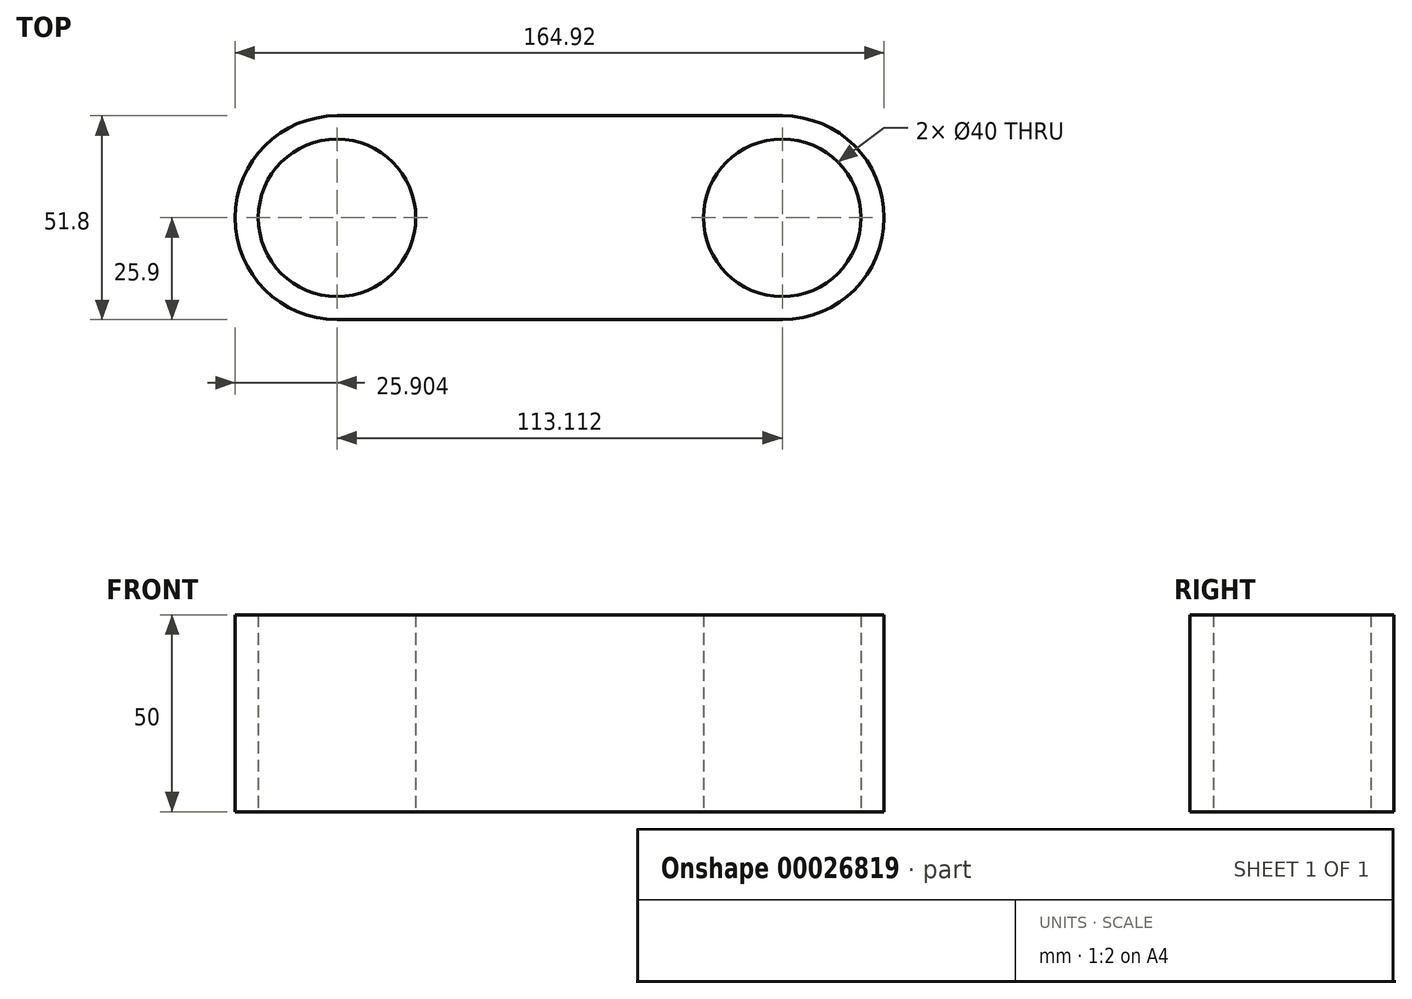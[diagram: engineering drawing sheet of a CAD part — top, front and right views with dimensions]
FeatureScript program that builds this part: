
annotation { "Feature Type Name" : "Feature", "Feature Type Description" : "" }
export const myFeature = defineFeature(function(context is Context, id is Id, definition is map)
    precondition{}
    {
        {
            var Q0;
            Q0=qCreatedBy(makeId("Top.planeOp"),FACE);
            var sketch = newSketch(context, id + "F0", { "sketchPlane" : qUnion([Q0])});
            skLineSegment(sketch, "E0.bottom", {"start": v(-64.63, 31.28) * mm, "end": v(48.49, 31.28) * mm});
            skLineSegment(sketch, "E0.top", {"start": v(-64.63, -20.52) * mm, "end": v(48.49, -20.52) * mm});
            skArc(sketch, "E1", {"start": v(-64.63, 31.28) * mm, "mid": v(-90.53, 5.38) * mm, "end": v(-64.63, -20.52) * mm});
            skArc(sketch, "E2", {"start": v(48.49, -20.52) * mm, "mid": v(74.39, 5.38) * mm, "end": v(48.49, 31.28) * mm});
            skCircle(sketch, "E3", {"center": v(-64.63, 5.38) * mm, "radius": 20 * mm});
            skCircle(sketch, "E4", {"center": v(48.49, 5.38) * mm, "radius": 20 * mm});
            skSolve(sketch);
        }
        {
            var Q0;
            Q0=makeQuery(id+"F0.imprint","IMPRINT",FACE,{"disambiguationData":[TD([[makeQuery(id+"F0.imprint","IMPRINT",EDGE,{"derivedFrom":sQuery(id+"F0.wireOp",EDGE,"E0.bottom")}),-1.0]])]});
            extrude(context, id + "F1", {"entities" : qUnion([Q0]), "depth" : 50 * mm});
        }
    });
